# Revit family: Hager-GAMMA-Surface_mounted-IP30-Without_Cover-With_DIN-Hosted-AT-de
name_source: partatom
category: Electrical Equipment
units: mm (PartAtom-declared; Revit-internal decimal feet)

## family parameters
Cut with Voids When Loaded = No
Host = Face
Maintain Annotation Orientation = Yes
Panel Configuration = Two Columns, Circuits Across
Part Type = Panelboard
Room Calculation Point = No
Round Connector Dimension = Use Diameter
Shared = No

## types (4) — shared parameters
BC_MODEL_ID = 1554265
BC_OBJECT_ID = 513847
BC_OBJECT_VERSION = #3
Code hager = ADD-EC000214_EU
EF000003 - Montageart = Aufputz
EF000007 - Farbe = weiß
EF000008 - Breite = 250 mm  [stored 0.82021 ft]
EF000024 - UV-beständig = No
EF000049 - Tiefe = 103 mm  [stored 0.337927 ft]
EF000116 - RAL-Nummer = 9010
EF000118 - Mit Montageplatte = No
EF001062 - EMV-Ausführung = No
EF001088 - Anbaumöglichkeit = Yes
EF001134 - DIN-Schiene = Yes
EF002950 - Breite in Teilungseinheiten = 13
EF004462 - Art der Schließung = sonstige
EF005474 - Schutzart (IP) = IP30
EF006244 - Transparenter Deckel/Tür = No
EF006306 - Mit Schloss = No
EF009212 - Ausführung Deckel = mit Ausschnitt
EF015776 - Erdungsklemmenblock = Yes
EF015941 - Signaldurchlassende Tür = Yes
ETIM class code = EC000214
ETIM class name = Small distribution board
HG000001-Anzahl der Spalten = 1
HG000002-Mit tür = No
HG000003-Bereich = GAMMA
HG000005-Dicke = 2 mm  [stored 0.00656168 ft]
HG000006-Unterputz = No
HG000009-Doppelflügeligen Tür = No
HG000010-Asymmetrische Türen = No
HG000011-Leere Reihen von unten = No
HG000012-Türschwenkwinkel = 90.00°
HG000013-Tür links = No
HG000014-Tür rechts = Yes
HG000015-Sichtbarkeit der Türöffnung = Yes
HG000016-3D-Türsichtbarkeit = Yes
HG000017-Distanz zwischen den Polen = 18 mm  [stored 0.0590551 ft]
HG000060-RAL-number = 9010
HG000099-Onfly Template ID-de-AT = 507532
HGEF0002950-Breite in Teilungseinheiten = 13
Manufacturer = Hager
Name = GAMMA-Surface_mounted-IP30-Without_Cover-With_DIN-AT
Name BIM&CO = Electricity
Name hager = ADD_Enclosures_EC000214
Uniformat = Low Tension Service & Dist.
Uniformat code = D501001
zero-valued in all types: Default Elevation, EF000218 - Einbautiefe, EF000332 - Einbauhöhe, EF000846 - Einbaubreite, EF001131 - Innentiefe, HG000007-Anzahl der leeren Spalten, HG000008-Anzahl der leeren Reihen

## per-type parameters (varying)
| type | BC_VARIANT_ID | EF000040 - Höhe | EF000266 - Anzahl der Reihen | EF015777 - Neutralleiterklemmenblock | HG000004-Herstellerreferenz | HGEF000266-Anzahl der Reihen |
| GAMMA-Surface_mounted_W250_H250_D103_13_Modular_Spacing-GD113G | 1178800 | 250 mm  [stored 0.82021 ft] | 1 | Yes | GD113G | 1 |
| GAMMA-Surface_mounted_W250_H375_D103_13_Modular_Spacing-GD213G | 1178802 | 375 mm  [stored 1.23031 ft] | 2 | No | GD213G | 2 |
| GAMMA-Surface_mounted_W250_H500_D103_13_Modular_Spacing-GD313G | 1178803 | 500 mm  [stored 1.64042 ft] | 3 | No | GD313G | 3 |
| GAMMA-Surface_mounted_W250_H625_D103_13_Modular_Spacing-GD413G | 1178804 | 625 mm  [stored 2.05052 ft] | 4 | No | GD413G | 4 |

note: column(s) folded — value = type name in every type: Reference

note: [stored X ft] marks values corroborated as IEEE doubles in the binary element streams (Revit-internal decimal feet)

## geometry (parser evidence)
native form markers: Sweep x14
no freeform markers — native parametric forms only
